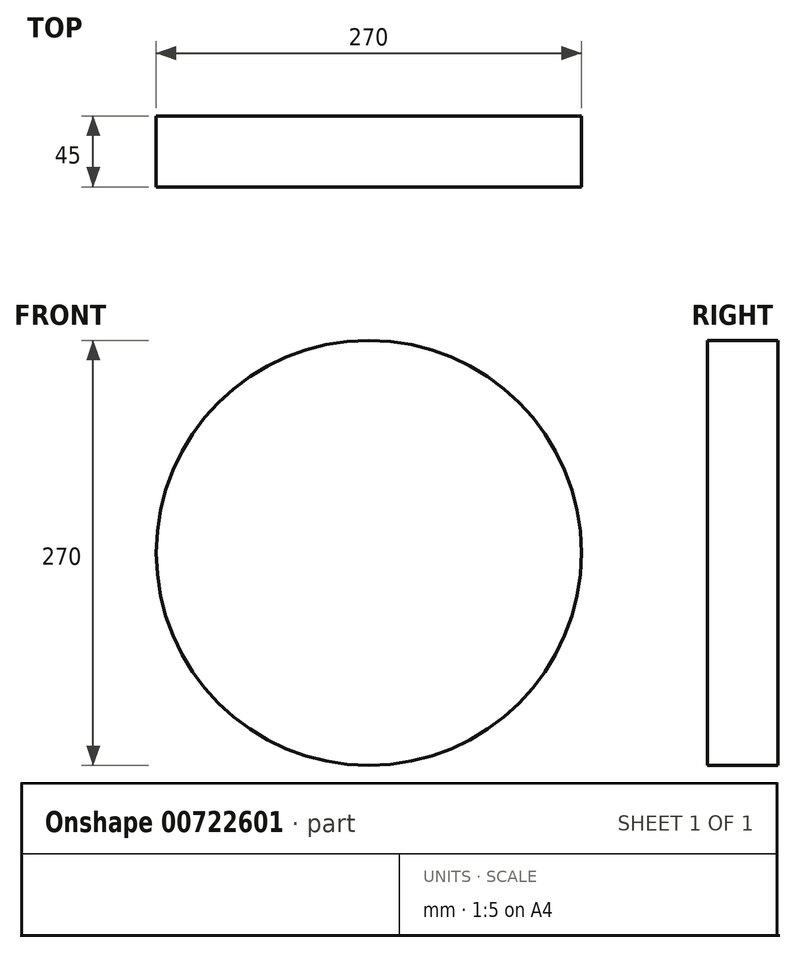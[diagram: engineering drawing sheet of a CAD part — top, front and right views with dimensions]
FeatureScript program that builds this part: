
annotation { "Feature Type Name" : "Feature", "Feature Type Description" : "" }
export const myFeature = defineFeature(function(context is Context, id is Id, definition is map)
    precondition{}
    {
        {
            var Q0;
            Q0=qCreatedBy(makeId("Front.planeOp"),FACE);
            var sketch = newSketch(context, id + "F0", { "sketchPlane" : qUnion([Q0])});
            skCircle(sketch, "E0", {"center": v(0, 0) * mm, "radius": 135 * mm});
            skSolve(sketch);
        }
        {
            var Q0;
            Q0=makeQuery(id+"F0.imprint","IMPRINT",FACE,{"disambiguationData":[TD([[makeQuery(id+"F0.imprint","IMPRINT",EDGE,{"derivedFrom":sQuery(id+"F0.wireOp",EDGE,"E0")}),1.0]])]});
            extrude(context, id + "F1", {"entities" : qUnion([Q0]), "depth" : 45 * mm, "offsetDistance" : 25 * mm});
        }
    });
